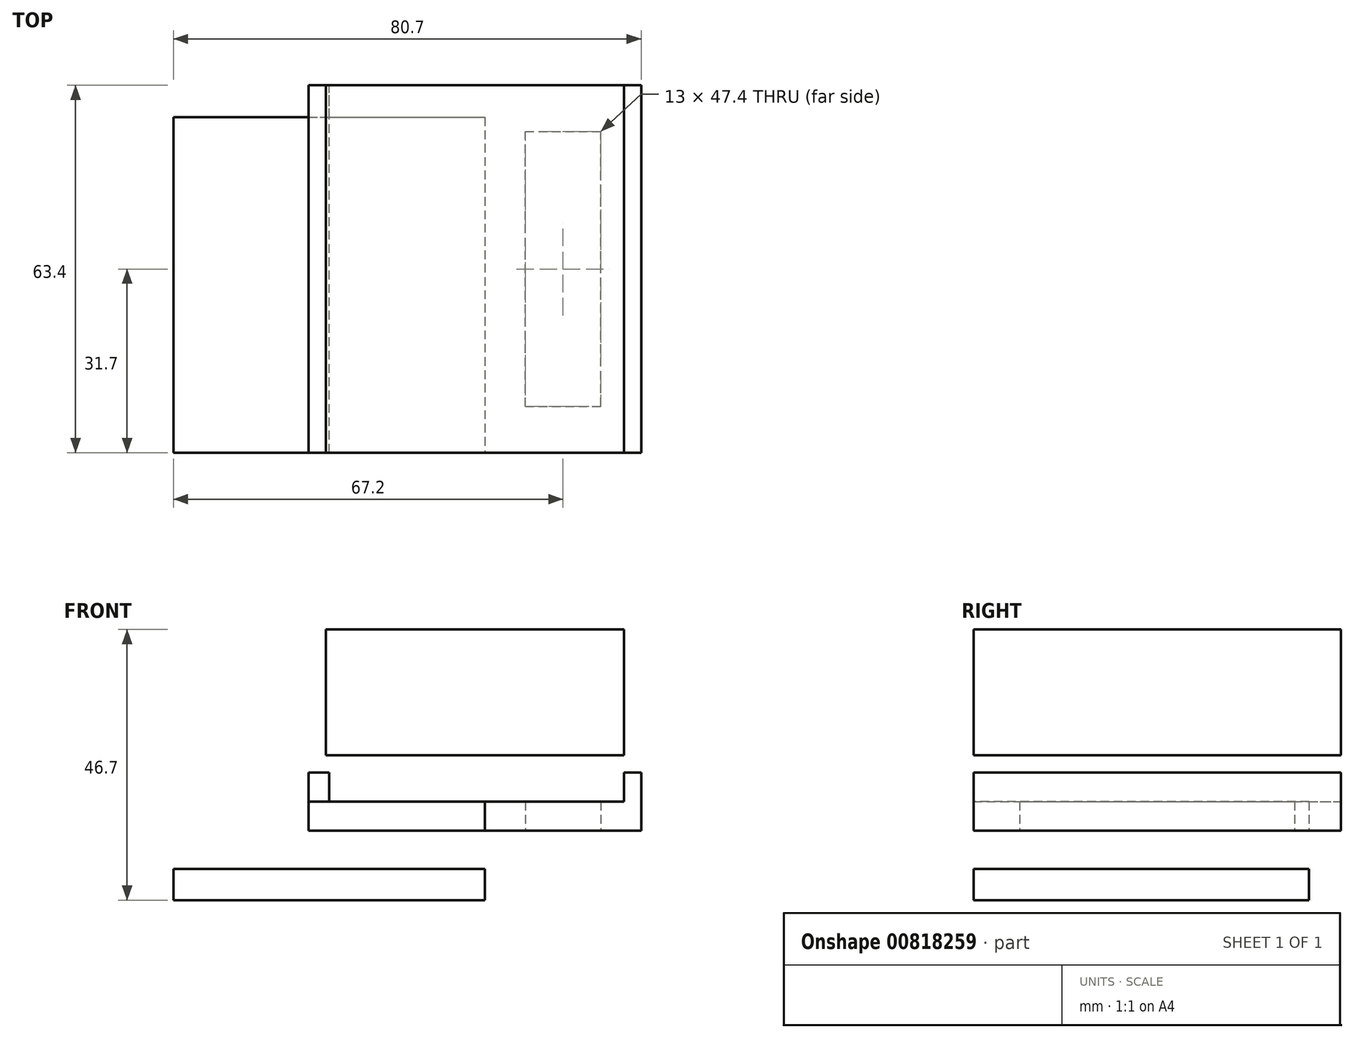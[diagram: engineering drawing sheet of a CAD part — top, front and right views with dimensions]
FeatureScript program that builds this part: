
annotation { "Feature Type Name" : "Feature", "Feature Type Description" : "" }
export const myFeature = defineFeature(function(context is Context, id is Id, definition is map)
    precondition{}
    {
        {
            var Q0;
            Q0=qCreatedBy(makeId("Top.planeOp"),FACE);
            var sketch = newSketch(context, id + "F0", { "sketchPlane" : qUnion([Q0])});
            skLineSegment(sketch, "E0.bottom", {"start": v(-26.85, 28.95) * mm, "end": v(26.85, 28.95) * mm});
            skLineSegment(sketch, "E0.top", {"start": v(-26.85, -28.95) * mm, "end": v(26.85, -28.95) * mm});
            skLineSegment(sketch, "E0.left", {"start": v(-26.85, 28.95) * mm, "end": v(-26.85, -28.95) * mm});
            skLineSegment(sketch, "E0.right", {"start": v(26.85, 28.95) * mm, "end": v(26.85, -28.95) * mm});
            skPoint(sketch, "E0.middle", {"position": v(0, 0) * mm});
            skSolve(sketch);
        }
        {
            var Q0;
            Q0 = qSketchRegion(id + "F0", true);
            extrude(context, id + "F1", {"entities" : qUnion([Q0]), "depth" : 5.4 * mm, "offsetDistance" : 25 * mm});
        }
        {
            var Q0;
            Q0=qCreatedBy(makeId("Top.planeOp"),FACE);
            cPlane(context, id + "F2", {"entities" : qUnion([Q0]), "cplaneType" : CPlaneType.OFFSET, "offset" : 25 * mm, "width" : 150 * mm, "height" : 150 * mm});
        }
        {
            var Q0;
            Q0=qCreatedBy(id+"F2.planeOp",FACE);
            var sketch = newSketch(context, id + "F3", { "sketchPlane" : qUnion([Q0])});
            skLineSegment(sketch, "E1.bottom", {"start": v(-0.55, 34.45) * mm, "end": v(50.85, 34.45) * mm});
            skLineSegment(sketch, "E1.top", {"start": v(-0.55, -28.95) * mm, "end": v(50.85, -28.95) * mm});
            skLineSegment(sketch, "E1.left", {"start": v(-0.55, 34.45) * mm, "end": v(-0.55, -28.95) * mm});
            skLineSegment(sketch, "E1.right", {"start": v(50.85, 34.45) * mm, "end": v(50.85, -28.95) * mm});
            skPoint(sketch, "E1.middle", {"position": v(25.15, 2.75) * mm});
            skLineSegment(sketch, "E2.0", {"start": v(-26.85, 28.95) * mm, "end": v(26.85, 28.95) * mm, "construction": true});
            skLineSegment(sketch, "E3.0", {"start": v(-26.85, 28.95) * mm, "end": v(-26.85, -28.95) * mm, "construction": true});
            skLineSegment(sketch, "E4.0", {"start": v(26.85, 28.95) * mm, "end": v(26.85, -28.95) * mm, "construction": true});
            skSolve(sketch);
        }
        {
            var Q0;
            Q0 = qSketchRegion(id + "F3", true);
            extrude(context, id + "F4", {"entities" : qUnion([Q0]), "depth" : 21.7 * mm, "offsetDistance" : 25 * mm});
        }
        {
            var Q0;
            Q0=qCreatedBy(makeId("Top.planeOp"),FACE);
            cPlane(context, id + "F5", {"entities" : qUnion([Q0]), "cplaneType" : CPlaneType.OFFSET, "offset" : 12 * mm, "width" : 150 * mm, "height" : 150 * mm});
        }
        {
            var Q0;
            Q0=qCreatedBy(id+"F5.planeOp",FACE);
            var sketch = newSketch(context, id + "F6", { "sketchPlane" : qUnion([Q0])});
            skLineSegment(sketch, "E5.0", {"start": v(26.85, 28.95) * mm, "end": v(26.85, -28.95) * mm});
            skLineSegment(sketch, "E6.0", {"start": v(50.85, 34.45) * mm, "end": v(50.85, -28.95) * mm});
            skLineSegment(sketch, "E7.0", {"start": v(-26.85, 28.95) * mm, "end": v(26.85, 28.95) * mm});
            skLineSegment(sketch, "E8.0", {"start": v(-0.55, 34.45) * mm, "end": v(-0.55, -28.95) * mm});
            skLineSegment(sketch, "E9.bottom", {"start": v(26.85, -28.95) * mm, "end": v(53.85, -28.95) * mm});
            skLineSegment(sketch, "E9.top", {"start": v(26.85, -24.95) * mm, "end": v(53.85, -24.95) * mm});
            skLineSegment(sketch, "E9.left", {"start": v(26.85, -28.95) * mm, "end": v(26.85, -24.95) * mm});
            skLineSegment(sketch, "E9.right", {"start": v(53.85, -28.95) * mm, "end": v(53.85, -24.95) * mm});
            skLineSegment(sketch, "E10.bottom", {"start": v(53.85, -24.95) * mm, "end": v(50.85, -24.95) * mm});
            skLineSegment(sketch, "E10.top", {"start": v(53.85, 34.45) * mm, "end": v(50.85, 34.45) * mm});
            skLineSegment(sketch, "E10.left", {"start": v(53.85, -24.95) * mm, "end": v(53.85, 34.45) * mm});
            skLineSegment(sketch, "E10.right", {"start": v(50.85, -24.95) * mm, "end": v(50.85, 34.45) * mm});
            skLineSegment(sketch, "E11.bottom", {"start": v(50.85, 34.45) * mm, "end": v(-3.55, 34.45) * mm});
            skLineSegment(sketch, "E11.top", {"start": v(50.85, 28.95) * mm, "end": v(-3.55, 28.95) * mm});
            skLineSegment(sketch, "E11.left", {"start": v(50.85, 34.45) * mm, "end": v(50.85, 28.95) * mm});
            skLineSegment(sketch, "E11.right", {"start": v(-3.55, 34.45) * mm, "end": v(-3.55, 28.95) * mm});
            skLineSegment(sketch, "E12.bottom", {"start": v(-3.55, 28.95) * mm, "end": v(-0.55, 28.95) * mm});
            skLineSegment(sketch, "E12.left", {"start": v(-3.55, 28.95) * mm, "end": v(-3.55, -28.95) * mm});
            skLineSegment(sketch, "E12.right", {"start": v(-0.55, 28.95) * mm, "end": v(-0.55, -28.95) * mm});
            skPoint(sketch, "E13", {"position": v(40.35, 2.75) * mm});
            skPoint(sketch, "E13.positionSnap0", {"position": v(50.85, 2.75) * mm});
            skPoint(sketch, "E13.positionSnap1", {"position": v(40.35, -24.95) * mm});
            skLineSegment(sketch, "E14.bottom", {"start": v(33.85, -20.95) * mm, "end": v(46.85, -20.95) * mm});
            skLineSegment(sketch, "E14.top", {"start": v(33.85, 26.45) * mm, "end": v(46.85, 26.45) * mm});
            skLineSegment(sketch, "E14.left", {"start": v(33.85, -20.95) * mm, "end": v(33.85, 26.45) * mm});
            skLineSegment(sketch, "E14.right", {"start": v(46.85, -20.95) * mm, "end": v(46.85, 26.45) * mm});
            skSolve(sketch);
        }
        {
            var Q0;
            {var subQ1=sQuery(id+"F6.wireOp",EDGE,"E9.right");var subQ6=sQuery(id+"F6.wireOp",EDGE,"E10.top");var subQ7=sQuery(id+"F6.wireOp",EDGE,"E11.top");var subQ16=sQuery(id+"F6.wireOp",EDGE,"E11.right");var subQ19=makeQuery(id+"F6.imprint","IMPRINT",EDGE,{"derivedFrom":subQ7});var subQ20=sQuery(id+"F6.wireOp",EDGE,"E5.0");var subQ24=sQuery(id+"F6.wireOp",EDGE,"E9.bottom");var subQ27=makeQuery(id+"F6.imprint","INTERSECT",VERTEX,{"derivedFrom":[subQ20,subQ24]});Q0=qUnion([makeQuery(id+"F6.imprint","IMPRINT",FACE,{"disambiguationData":[TD([[subQ19,-1.0]])]}),makeQuery(id+"F6.imprint","IMPRINT",FACE,{"disambiguationData":[TD([[makeQuery(id+"F6.imprint","IMPRINT",EDGE,{"disambiguationData":[TD([[subQ27,1.0]])],"derivedFrom":subQ20}),1.0]])]}),makeQuery(id+"F6.imprint","IMPRINT",FACE,{"disambiguationData":[TD([[makeQuery(id+"F6.imprint","IMPRINT",EDGE,{"derivedFrom":subQ1}),1.0]])]}),makeQuery(id+"F6.imprint","IMPRINT",FACE,{"disambiguationData":[TD([[subQ19,1.0]])]}),makeQuery(id+"F6.imprint","IMPRINT",FACE,{"disambiguationData":[TD([[makeQuery(id+"F6.imprint","IMPRINT",EDGE,{"derivedFrom":subQ16}),1.0]])]}),makeQuery(id+"F6.imprint","IMPRINT",FACE,{"disambiguationData":[TD([[makeQuery(id+"F6.imprint","IMPRINT",EDGE,{"derivedFrom":subQ6}),1.0]])]})]);}
            extrude(context, id + "F7", {"entities" : qUnion([Q0]), "depth" : 5 * mm, "offsetDistance" : 25 * mm});
        }
        {
            var Q0;
            {var subQ4=sQuery(id+"F6.wireOp",EDGE,"E10.top");Q0=makeQuery(id+"F6.imprint","IMPRINT",FACE,{"disambiguationData":[TD([[makeQuery(id+"F6.imprint","IMPRINT",EDGE,{"derivedFrom":subQ4}),1.0]])]});}
            var Q1;
            {var subQ5=sQuery(id+"F6.wireOp",EDGE,"E9.right");Q1=makeQuery(id+"F6.imprint","IMPRINT",FACE,{"disambiguationData":[TD([[makeQuery(id+"F6.imprint","IMPRINT",EDGE,{"derivedFrom":subQ5}),1.0]])]});}
            var Q2;
            {var subQ3=sQuery(id+"F6.wireOp",EDGE,"E11.right");Q2=makeQuery(id+"F6.imprint","IMPRINT",FACE,{"disambiguationData":[TD([[makeQuery(id+"F6.imprint","IMPRINT",EDGE,{"derivedFrom":subQ3}),1.0]])]});}
            extrude(context, id + "F8", {"entities" : qUnion([Q0, Q1, Q2]), "operationType" : NewBodyOperationType.ADD, "depth" : 10 * mm, "offsetDistance" : 25 * mm});
        }
        {
            var Q0;
            Q0=qCreatedBy(id+"F5.planeOp",FACE);
            cPlane(context, id + "F9", {"entities" : qUnion([Q0]), "cplaneType" : CPlaneType.OFFSET, "offset" : 5 * mm, "width" : 150 * mm, "height" : 150 * mm});
        }
        {
            var Q0;
            Q0=qCreatedBy(id+"F9.planeOp",FACE);
            var sketch = newSketch(context, id + "F10", { "sketchPlane" : qUnion([Q0])});
            skPoint(sketch, "E15.0", {"position": v(-3.55, -28.95) * mm});
            skPoint(sketch, "E16.0", {"position": v(0, 28.95) * mm});
            skLineSegment(sketch, "E17.bottom", {"start": v(-3.55, -28.95) * mm, "end": v(0, -28.95) * mm});
            skLineSegment(sketch, "E17.top", {"start": v(-3.55, 28.95) * mm, "end": v(0, 28.95) * mm});
            skLineSegment(sketch, "E17.left", {"start": v(-3.55, -28.95) * mm, "end": v(-3.55, 28.95) * mm});
            skLineSegment(sketch, "E17.right", {"start": v(0, -28.95) * mm, "end": v(0, 28.95) * mm});
            skPoint(sketch, "E18.0", {"position": v(-3.55, 34.45) * mm});
            skLineSegment(sketch, "E19.bottom", {"start": v(-3.55, 34.45) * mm, "end": v(0, 34.45) * mm});
            skLineSegment(sketch, "E19.left", {"start": v(-3.55, 34.45) * mm, "end": v(-3.55, 28.95) * mm});
            skLineSegment(sketch, "E19.right", {"start": v(0, 34.45) * mm, "end": v(0, 28.95) * mm});
            skSolve(sketch);
        }
        {
            var Q0;
            Q0 = qSketchRegion(id + "F10", true);
            extrude(context, id + "F11", {"entities" : qUnion([Q0]), "operationType" : NewBodyOperationType.ADD, "depth" : 5 * mm, "offsetDistance" : 25 * mm});
        }
    });
